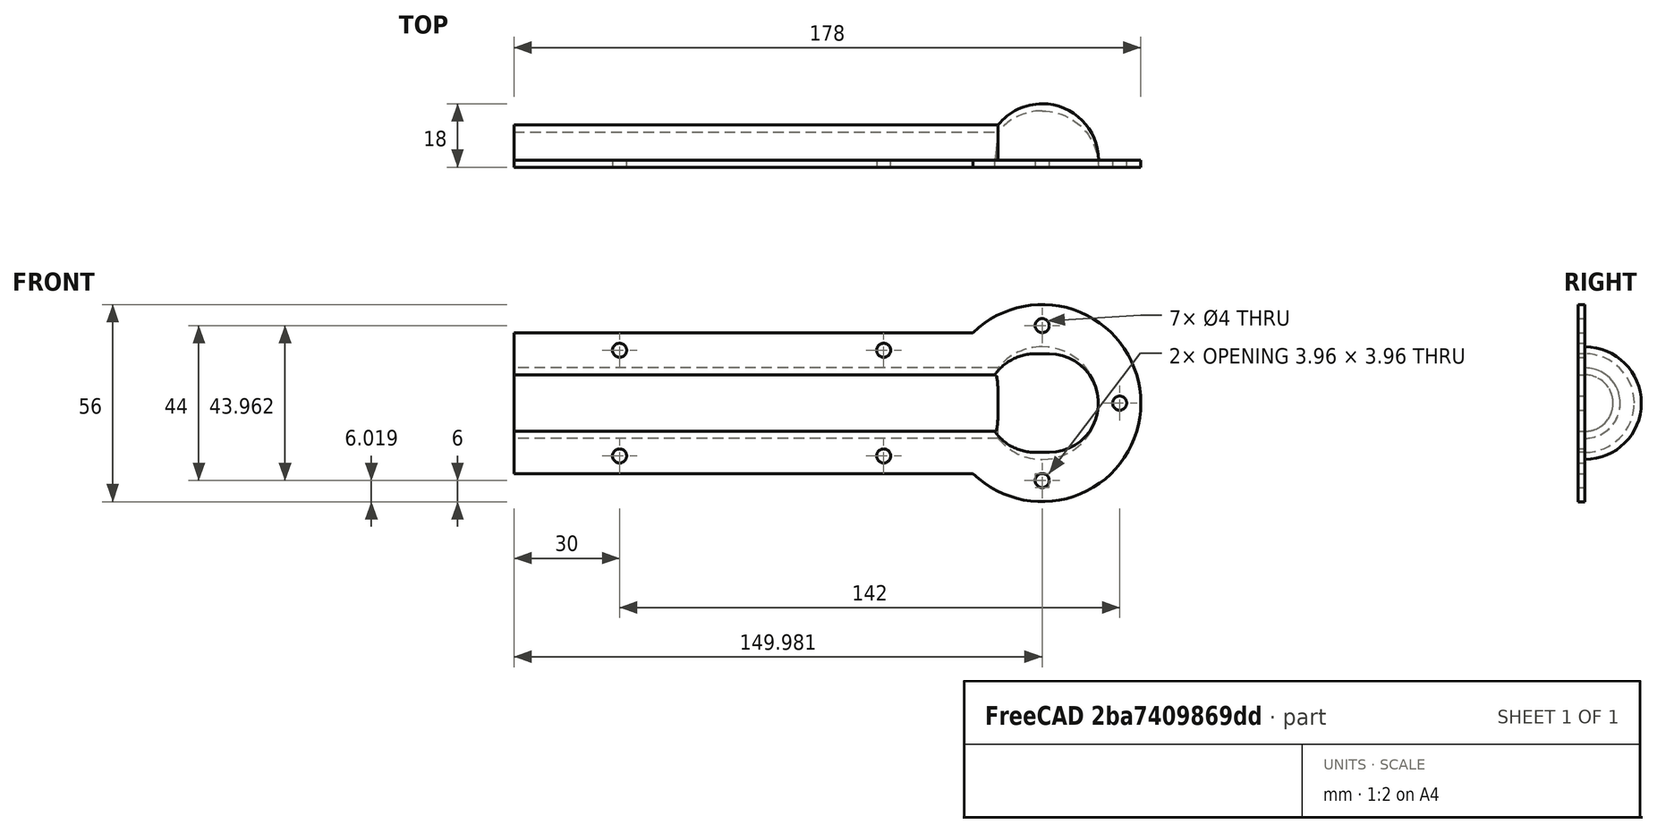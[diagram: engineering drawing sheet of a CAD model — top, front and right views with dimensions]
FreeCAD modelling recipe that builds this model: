
FCSTD DOCUMENT  (FreeCAD 0.20R)
Label: cache_fils_V1
License: All rights reserved
LicenseURL: http://en.wikipedia.org/wiki/All_rights_reserved
objects: Sketcher::SketchObject×5, PartDesign::Pocket×2, PartDesign::Revolution×1, PartDesign::Pad×1, PartDesign::Groove×1, PartDesign::Body×1, Mesh::Feature×1
note: 16 computed .brp shape members not serialized (recipe doc carries the construction recipe); baked Part::Feature solids carry a one-line shape summary decoded from their .brp

FEATURE [Sketcher::SketchObject] Sketch
  FullyConstrained = true
  MapMode = 5
  Support = -> [XY_Plane]
  sketch-geometry (7):
    g0: ArcOfCircle CenterX=0 CenterY=2 CenterZ=0 NormalX=0 NormalY=0 NormalZ=1 AngleXU=0 Radius=16 StartAngle=1e-16 EndAngle=1.5708
    g1: ArcOfCircle CenterX=0 CenterY=2 CenterZ=0 NormalX=0 NormalY=0 NormalZ=1 AngleXU=0 Radius=14 StartAngle=1e-16 EndAngle=1.5708
    g2: LineSegment StartX=14 StartY=2 StartZ=0 EndX=14 EndY=0 EndZ=0
    g3: LineSegment StartX=14 StartY=0 StartZ=0 EndX=28 EndY=0 EndZ=0
    g4: LineSegment StartX=28 StartY=0 StartZ=0 EndX=28 EndY=2 EndZ=0
    g5: LineSegment StartX=28 StartY=2 StartZ=0 EndX=16 EndY=2 EndZ=0
    g6: LineSegment StartX=9e-16 StartY=16 StartZ=0 EndX=1e-15 EndY=18 EndZ=0
  constraints (21):
    c: PointOnObject(g0,g-2)
    c: PointOnObject(g0,g-2)
    c: Coincident(g1,g0)
    c: PointOnObject(g1,g-2)
    c: Tangent(g1,g2) = 1.5708
    c: Coincident(g2,g3)
    c: PointOnObject(g3,g-1)
    c: Horizontal(g3)
    c: Coincident(g3,g4)
    c: Vertical(g4)
    c: Coincident(g4,g5)
    c: Coincident(g5,g0)
    c: Horizontal(g5)
    c: Perpendicular(g3,g2)
    c: Radius(g1) = 14
    c: Radius(g0) = 16
    c: DistanceY(g4,g4) = 2
    c: DistanceY(g2,g2) = 2
    c: DistanceX(g5,g5) = 12
    c: Coincident(g6,g1)
    c: Coincident(g6,g0)
FEATURE [PartDesign::Revolution] Revolution
  Angle = 360
  Axis = (0,1,0)
  Base = (0,0,0)
  Profile = -> Sketch
  ReferenceAxis = -> Sketch [V_Axis]
  Reversed = true
FEATURE [Sketcher::SketchObject] Sketch001
  FullyConstrained = true
  MapMode = 5
  Placement = pos=(0,0,0) rot=(0.57735,0.57735,0.57735;2.0944rad)
  Support = -> [YZ_Plane]
  sketch-geometry (6):
    g0: ArcOfCircle CenterX=2 CenterY=-5e-16 CenterZ=0 NormalX=0 NormalY=0 NormalZ=1 AngleXU=0 Radius=10 StartAngle=4.71239 EndAngle=7.85398
    g1: LineSegment StartX=2 StartY=10 StartZ=0 EndX=0 EndY=10 EndZ=0
    g2: LineSegment StartX=0 StartY=10 StartZ=0 EndX=0 EndY=-10 EndZ=0
    g3: GeomPoint X=0 Y=-10 Z=0
    g4: GeomPoint X=2 Y=-10 Z=0
    g5: LineSegment StartX=0 StartY=-10 StartZ=0 EndX=2 EndY=-10 EndZ=0
  constraints (13):
    c: Tangent(g0,g1) = -1.5708
    c: Coincident(g1,g2)
    c: Vertical(g2)
    c: Coincident(g3,g2)
    c: Coincident(g4,g0)
    c: Symmetric(g0,g0,g-1)
    c: Radius(g0) = 10
    c: Angle(g0) = 3.14159
    c: DistanceX(g1,g1) = 2
    c: PointOnObject(g1,g-2)
    c: Coincident(g5,g2)
    c: Coincident(g5,g0)
    c: Horizontal(g5)
FEATURE [PartDesign::Pocket] Pocket
  BaseFeature = -> Revolution
  Length = 38
  Length2 = 100
  Profile = -> Sketch001
  Type = 0
FEATURE [Sketcher::SketchObject] Sketch002
  ExternalGeometry = -> [Pocket]
  FullyConstrained = false
  MapMode = 5
  Placement = pos=(0,0,0) rot=(0.57735,0.57735,0.57735;2.0944rad)
  Support = -> [YZ_Plane]
  sketch-geometry (12):
    g0: ArcOfCircle CenterX=2 CenterY=-7.1e-15 CenterZ=0 NormalX=0 NormalY=0 NormalZ=1 AngleXU=0 Radius=10 StartAngle=4.71239 EndAngle=7.85398
    g1: ArcOfCircle CenterX=2 CenterY=-7.1e-15 CenterZ=0 NormalX=0 NormalY=0 NormalZ=1 AngleXU=0 Radius=8 StartAngle=4.71239 EndAngle=7.85398
    g2: LineSegment StartX=2 StartY=-10 StartZ=0 EndX=2 EndY=-20 EndZ=0
    g3: LineSegment StartX=2 StartY=-20 StartZ=0 EndX=0 EndY=-20 EndZ=0
    g4: LineSegment StartX=0 StartY=-20 StartZ=0 EndX=0 EndY=-8 EndZ=0
    g5: LineSegment StartX=0 StartY=-8 StartZ=0 EndX=2 EndY=-8 EndZ=0
    g6: LineSegment StartX=2 StartY=10 StartZ=0 EndX=2 EndY=20 EndZ=0
    g7: LineSegment StartX=2 StartY=20 StartZ=0 EndX=0 EndY=20 EndZ=0
    g8: LineSegment StartX=0 StartY=20 StartZ=0 EndX=0 EndY=8 EndZ=0
    g9: LineSegment StartX=0 StartY=8 StartZ=0 EndX=2 EndY=8 EndZ=0
    g10: GeomPoint X=2 Y=28 Z=0
    g11: GeomPoint X=2 Y=28 Z=0
  constraints (31):
    c: Coincident(g0,g-4)
    c: PointOnObject(g0,g-4)
    c: Radius(g0) = 10
    c: Coincident(g1,g0)
    c: PointOnObject(g1,g-4)
    c: Radius(g1) = 8
    c: PointOnObject(g1,g-6)
    c: Coincident(g0,g2)
    c: Coincident(g3,g4)
    c: PointOnObject(g4,g-2)
    c: Coincident(g4,g5)
    c: Coincident(g5,g1)
    c: Horizontal(g5)
    c: Horizontal(g3)
    c: Coincident(g0,g6)
    c: PointOnObject(g7,g-2)
    c: Coincident(g7,g8)
    c: PointOnObject(g8,g-2)
    c: Coincident(g8,g9)
    c: Coincident(g9,g1)
    c: Horizontal(g9)
    c: Horizontal(g7)
    c: Coincident(g11,g-4)
    c: Vertical(g2)
    c: PointOnObject(g3,g-2)
    c: Coincident(g2,g3)
    c: PointOnObject(g2,g-6)
    c: DistanceY(g2,g2) = 10
    c: Coincident(g6,g7)
    c: Vertical(g6)
    c: DistanceY(g6,g6) = 10
FEATURE [PartDesign::Pad] Pad
  BaseFeature = -> Pocket
  Direction = (1,-2e-16,3e-16)
  Length = 150
  Length2 = 100
  Profile = -> Sketch002
  Reversed = true
  Type = 0
FEATURE [Sketcher::SketchObject] Sketch003
  ExternalGeometry = -> [Pad]
  FullyConstrained = true
  MapMode = 5
  Placement = pos=(0,0,0) rot=(0.57735,0.57735,0.57735;2.0944rad)
  Support = -> [Pad]
  sketch-geometry (4):
    g0: ArcOfCircle CenterX=2 CenterY=-6.2e-15 CenterZ=0 NormalX=0 NormalY=0 NormalZ=1 AngleXU=0 Radius=14 StartAngle=4.71239 EndAngle=7.85398
    g1: LineSegment StartX=2 StartY=14 StartZ=0 EndX=3.1e-15 EndY=14 EndZ=0
    g2: LineSegment StartX=3.1e-15 StartY=14 StartZ=0 EndX=3.1e-15 EndY=-14 EndZ=0
    g3: LineSegment StartX=3.1e-15 StartY=-14 StartZ=0 EndX=2 EndY=-14 EndZ=0
  constraints (11):
    c: Coincident(g0,g-8)
    c: PointOnObject(g0,g-7)
    c: Radius(g0) = 14
    c: PointOnObject(g0,g-13)
    c: Tangent(g0,g1) = -1.5708
    c: Coincident(g1,g2)
    c: PointOnObject(g2,g-5)
    c: Vertical(g2)
    c: Coincident(g2,g3)
    c: Coincident(g3,g0)
    c: Horizontal(g3)
FEATURE [PartDesign::Groove] Groove
  Angle = 360
  Axis = (-2e-16,0,1)
  Base = (0,0,0)
  BaseFeature = -> Pad
  Profile = -> Sketch003
  ReferenceAxis = -> Sketch003 [V_Axis]
FEATURE [Sketcher::SketchObject] Sketch004
  FullyConstrained = true
  MapMode = 5
  Placement = pos=(0,2,0) rot=(0,0.707107,0.707107;3.14159rad)
  Support = -> [Groove]
  sketch-geometry (12):
    g0: Circle CenterX=0 CenterY=22 CenterZ=0 NormalX=0 NormalY=0 NormalZ=1 AngleXU=0 Radius=2
    g1: Circle CenterX=0 CenterY=-22 CenterZ=0 NormalX=0 NormalY=0 NormalZ=1 AngleXU=0 Radius=2
    g2: Circle CenterX=-22 CenterY=0 CenterZ=0 NormalX=0 NormalY=0 NormalZ=1 AngleXU=0 Radius=2
    g3: Circle CenterX=45 CenterY=15 CenterZ=0 NormalX=0 NormalY=0 NormalZ=1 AngleXU=0 Radius=2
    g4: Circle CenterX=120 CenterY=15 CenterZ=0 NormalX=0 NormalY=0 NormalZ=1 AngleXU=0 Radius=2
    g5: Circle CenterX=45 CenterY=-15 CenterZ=0 NormalX=0 NormalY=0 NormalZ=1 AngleXU=0 Radius=2
    g6: Circle CenterX=120 CenterY=-15 CenterZ=0 NormalX=0 NormalY=0 NormalZ=1 AngleXU=0 Radius=2
    g7: Circle CenterX=0 CenterY=0 CenterZ=0 NormalX=0 NormalY=0 NormalZ=1 AngleXU=0 Radius=22
    g8: LineSegment StartX=0 StartY=15 StartZ=0 EndX=120 EndY=15 EndZ=0
    g9: LineSegment StartX=120 StartY=15 StartZ=0 EndX=120 EndY=-15 EndZ=0
    g10: LineSegment StartX=120 StartY=-15 StartZ=0 EndX=0 EndY=-15 EndZ=0
    g11: LineSegment StartX=0 StartY=-15 StartZ=0 EndX=0 EndY=15 EndZ=0
  constraints (31):
    c: PointOnObject(g0,g-2)
    c: PointOnObject(g1,g-2)
    c: PointOnObject(g2,g-1)
    c: Radius(g6) = 2
    c: Equal(g6,g4)
    c: Equal(g6,g3)
    c: Equal(g6,g5)
    c: Equal(g6,g1)
    c: Equal(g6,g2)
    c: Equal(g6,g0)
    c: Coincident(g7,g-1)
    c: Radius(g7) = 22
    c: PointOnObject(g0,g7)
    c: PointOnObject(g2,g7)
    c: PointOnObject(g1,g7)
    c: Coincident(g8,g9)
    c: Coincident(g9,g10)
    c: Coincident(g10,g11)
    c: Coincident(g11,g8)
    c: Horizontal(g8)
    c: Horizontal(g10)
    c: Vertical(g9)
    c: Symmetric(g10,g8,g-1)
    c: DistanceY(g-1,g8) = 15
    c: Symmetric(g5,g3,g-1)
    c: Symmetric(g4,g6,g-1)
    c: DistanceY(g-1,g3) = 15
    c: Coincident(g4,g8)
    c: DistanceX(g8,g8) = 120
    c: DistanceX(g-2,g3) = 45
    c: PointOnObject(g8,g-2)
FEATURE [PartDesign::Pocket] Pocket001
  BaseFeature = -> Groove
  Length = 5
  Length2 = 100
  Profile = -> Sketch004
  Type = 0
FEATURE [PartDesign::Body] Body
  Group = -> [Sketch,Revolution,Sketch001,Pocket,Sketch002,Pad,Sketch003,Groove,Sketch004,Pocket001]
  Origin = -> Origin
  Tip = -> Pocket001
FEATURE [Mesh::Feature] Mesh  label="Body (Meshed)"
